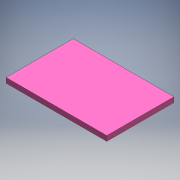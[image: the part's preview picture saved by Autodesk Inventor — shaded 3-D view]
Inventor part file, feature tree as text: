
AUTODESK INVENTOR PART (.ipt)
format: ipt  version: 2016 (Build 200138000, 138)  size: 100,352 bytes
history: native  units: mm
features: extrude x1, sketch x1
ambient origin geometry x8: Origin, YZ Plane, XZ Plane, XY Plane, X Axis, Y Axis, Z Axis, Center Point
bodies: Solid1 (feature_tree)
feature tree (2):
  extrude  "Extrusion1"  Depth=1.5mm
  sketch  "Sketch1"  dims[d0=20.0mm d1=10.0mm d2=30.0mm d3=15.0mm d4=1.5mm d5=0.0mm]
